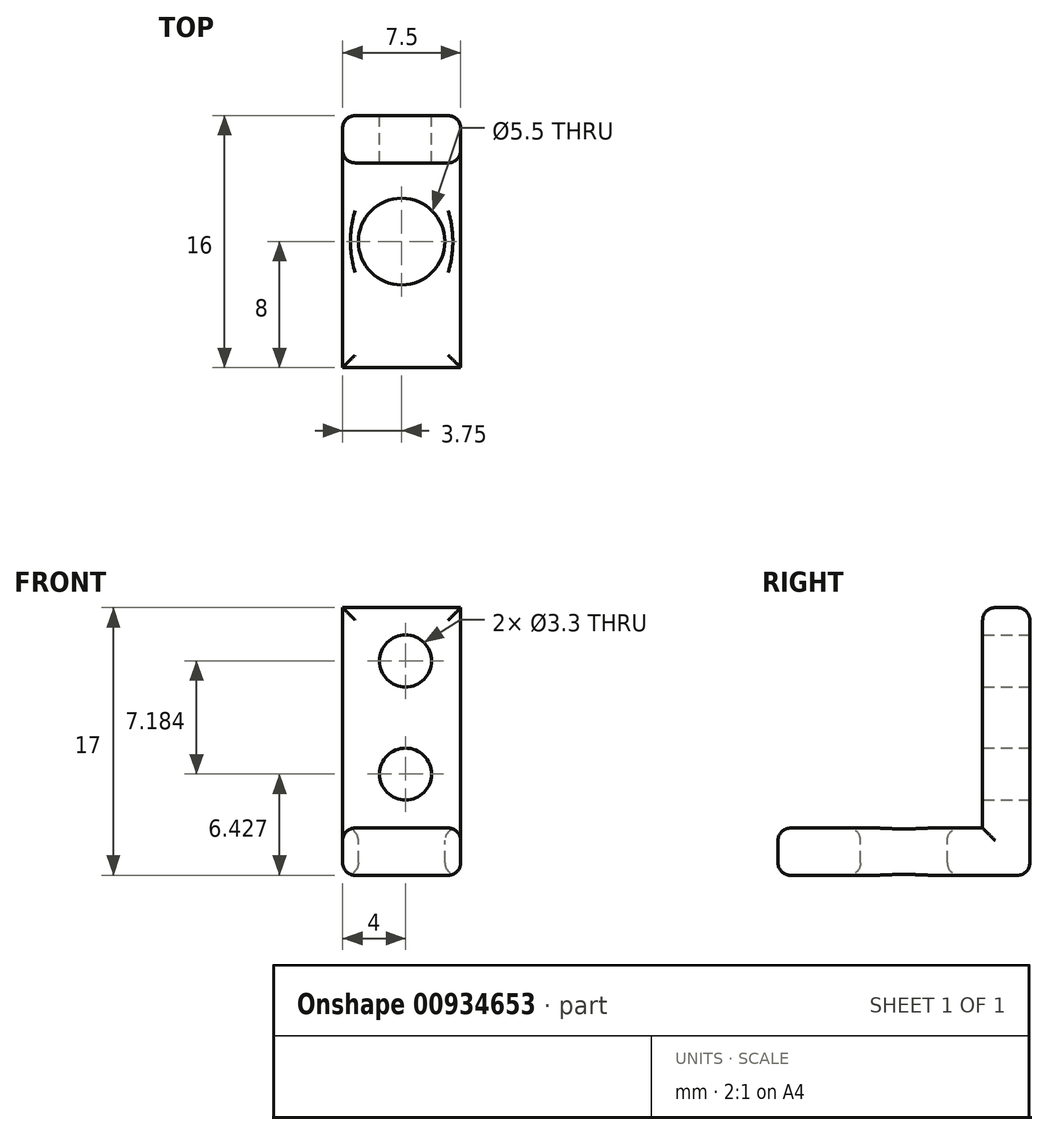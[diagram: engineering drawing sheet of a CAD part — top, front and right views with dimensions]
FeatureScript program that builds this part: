
annotation { "Feature Type Name" : "Feature", "Feature Type Description" : "" }
export const myFeature = defineFeature(function(context is Context, id is Id, definition is map)
    precondition{}
    {
        {
            var Q0;
            Q0=qCreatedBy(makeId("Top.planeOp"),FACE);
            var sketch = newSketch(context, id + "F0", { "sketchPlane" : qUnion([Q0])});
            skLineSegment(sketch, "E0.bottom", {"start": v(0, 0) * mm, "end": v(7.5, 0) * mm});
            skLineSegment(sketch, "E0.top", {"start": v(0, 16) * mm, "end": v(7.5, 16) * mm});
            skLineSegment(sketch, "E0.left", {"start": v(0, 0) * mm, "end": v(0, 16) * mm});
            skLineSegment(sketch, "E0.right", {"start": v(7.5, 0) * mm, "end": v(7.5, 16) * mm});
            skPoint(sketch, "E0.middle", {"position": v(3.75, 8) * mm});
            skCircle(sketch, "E1", {"center": v(3.75, 8) * mm, "radius": 2.75 * mm});
            skSolve(sketch);
        }
        {
            var Q0;
            Q0=makeQuery(id+"F0.imprint","IMPRINT",FACE,{"disambiguationData":[TD([[makeQuery(id+"F0.imprint","IMPRINT",EDGE,{"derivedFrom":sQuery(id+"F0.wireOp",EDGE,"E0.bottom")}),1.0]])]});
            var sketch = newSketch(context, id + "F1", { "sketchPlane" : qUnion([Q0])});
            skLineSegment(sketch, "E2.bottom", {"start": v(0, 13) * mm, "end": v(7.5, 13) * mm});
            skLineSegment(sketch, "E2.top", {"start": v(0, 16) * mm, "end": v(7.5, 16) * mm});
            skLineSegment(sketch, "E2.left", {"start": v(0, 13) * mm, "end": v(0, 16) * mm});
            skLineSegment(sketch, "E2.right", {"start": v(7.5, 13) * mm, "end": v(7.5, 16) * mm});
            skSolve(sketch);
        }
        {
            var Q0;
            Q0 = qSketchRegion(id + "F1", true);
            extrude(context, id + "F2", {"entities" : qUnion([Q0]), "depth" : 14 * mm, "offsetDistance" : 25 * mm});
        }
        {
            var Q0;
            Q0=makeQuery(id+"F0.imprint","IMPRINT",FACE,{"disambiguationData":[TD([[makeQuery(id+"F0.imprint","IMPRINT",EDGE,{"derivedFrom":sQuery(id+"F0.wireOp",EDGE,"E0.bottom")}),1.0]])]});
            extrude(context, id + "F3", {"entities" : qUnion([Q0]), "operationType" : NewBodyOperationType.ADD, "oppositeDirection" : true, "depth" : 3 * mm, "offsetDistance" : 25 * mm});
        }
        {
            var Q0;
            Q0=makeQuery(id+"F3.boolean.opBoolean","MERGE",FACE,{"derivedFrom":[makeQuery(id+"F2.opExtrude","SWEPT_FACE",FACE,{"disambiguationData":[OSD([sQuery(id+"F1.wireOp",EDGE,"E2.top")])]}),makeQuery(id+"F3.opExtrude","SWEPT_FACE",FACE,{"disambiguationData":[OSD([sQuery(id+"F0.wireOp",EDGE,"E0.top")])]})]});
            var sketch = newSketch(context, id + "F4", { "sketchPlane" : qUnion([Q0])});
            skCircle(sketch, "E3", {"center": v(-4, 3.43) * mm, "radius": 1.65 * mm});
            skCircle(sketch, "E4", {"center": v(-4, 10.61) * mm, "radius": 1.65 * mm});
            skSolve(sketch);
        }
        {
            var Q0;
            Q0 = qSketchRegion(id + "F4", true);
            extrude(context, id + "F5", {"entities" : qUnion([Q0]), "operationType" : NewBodyOperationType.REMOVE, "oppositeDirection" : true, "depth" : 25 * mm, "offsetDistance" : 25 * mm});
        }
        {
            var Q0;
            Q0=makeQuery(id+"F2.opExtrude","CAP_EDGE",EDGE,{"disambiguationData":[OSD([sQuery(id+"F1.wireOp",EDGE,"E2.top")])],"isStart":false});
            var Q1;
            Q1=makeQuery(id+"F2.opExtrude","CAP_EDGE",EDGE,{"disambiguationData":[OSD([sQuery(id+"F1.wireOp",EDGE,"E2.bottom")])],"isStart":false});
            var Q2;
            Q2=makeQuery(id+"F3.opExtrude","CAP_EDGE",EDGE,{"disambiguationData":[OSD([sQuery(id+"F0.wireOp",EDGE,"E0.bottom")])],"isStart":true});
            var Q3;
            Q3=makeQuery(id+"F3.opExtrude","CAP_EDGE",EDGE,{"disambiguationData":[OSD([sQuery(id+"F0.wireOp",EDGE,"E0.top")])],"isStart":false});
            var Q4;
            Q4=makeQuery(id+"F3.opExtrude","CAP_EDGE",EDGE,{"disambiguationData":[OSD([sQuery(id+"F0.wireOp",EDGE,"E0.bottom")])],"isStart":false});
            var Q5;
            Q5=makeQuery(id+"F5.boolean.opBoolean","COPY",EDGE,{"derivedFrom":makeQuery(id+"F5.opExtrude","CAP_EDGE",EDGE,{"disambiguationData":[OSD([sQuery(id+"F4.wireOp",EDGE,"E4")])],"isStart":true})});
            var Q6;
            Q6=makeQuery(id+"F5.boolean.opBoolean","COPY",EDGE,{"derivedFrom":makeQuery(id+"F5.opExtrude","CAP_EDGE",EDGE,{"disambiguationData":[OSD([sQuery(id+"F4.wireOp",EDGE,"E3")])],"isStart":true})});
            var Q7;
            Q7=makeQuery(id+"F3.opExtrude","CAP_EDGE",EDGE,{"disambiguationData":[OSD([sQuery(id+"F0.wireOp",EDGE,"E1")])],"isStart":false});
            var Q8;
            Q8=makeQuery(id+"F3.opExtrude","CAP_EDGE",EDGE,{"disambiguationData":[OSD([sQuery(id+"F0.wireOp",EDGE,"E1")])],"isStart":true});
            var Q9;
            Q9=makeQuery(id+"F3.boolean.opBoolean","MERGE",EDGE,{"derivedFrom":[makeQuery(id+"F2.opExtrude","SWEPT_EDGE",EDGE,{"disambiguationData":[OSD([sQuery(id+"F1.wireOp",EDGE,"E2.top"),sQuery(id+"F1.wireOp",EDGE,"E2.left")])]}),makeQuery(id+"F3.opExtrude","SWEPT_EDGE",EDGE,{"disambiguationData":[OSD([sQuery(id+"F0.wireOp",EDGE,"E0.top"),sQuery(id+"F0.wireOp",EDGE,"E0.left")])]})]});
            var Q10;
            Q10=makeQuery(id+"F3.boolean.opBoolean","MERGE",EDGE,{"derivedFrom":[makeQuery(id+"F2.opExtrude","SWEPT_EDGE",EDGE,{"disambiguationData":[OSD([sQuery(id+"F1.wireOp",EDGE,"E2.top"),sQuery(id+"F1.wireOp",EDGE,"E2.right")])]}),makeQuery(id+"F3.opExtrude","SWEPT_EDGE",EDGE,{"disambiguationData":[OSD([sQuery(id+"F0.wireOp",EDGE,"E0.top"),sQuery(id+"F0.wireOp",EDGE,"E0.right")])]})]});
            var Q11;
            Q11=makeQuery(id+"F3.opExtrude","CAP_EDGE",EDGE,{"disambiguationData":[OSD([sQuery(id+"F0.wireOp",EDGE,"E0.left")])],"isStart":false});
            var Q12;
            Q12=makeQuery(id+"F3.opExtrude","CAP_EDGE",EDGE,{"disambiguationData":[OSD([sQuery(id+"F0.wireOp",EDGE,"E0.right")])],"isStart":false});
            var Q13;
            Q13=makeQuery(id+"F3.opExtrude","CAP_EDGE",EDGE,{"disambiguationData":[OSD([sQuery(id+"F0.wireOp",EDGE,"E0.left")])],"isStart":true});
            var Q14;
            Q14=makeQuery(id+"F2.opExtrude","SWEPT_EDGE",EDGE,{"disambiguationData":[OSD([sQuery(id+"F0.wireOp",EDGE,"E0.left"),sQuery(id+"F1.wireOp",EDGE,"E2.bottom"),sQuery(id+"F1.wireOp",EDGE,"E2.left")])]});
            var Q15;
            Q15=makeQuery(id+"F3.opExtrude","CAP_EDGE",EDGE,{"disambiguationData":[OSD([sQuery(id+"F0.wireOp",EDGE,"E0.right")])],"isStart":true});
            var Q16;
            Q16=makeQuery(id+"F2.opExtrude","SWEPT_EDGE",EDGE,{"disambiguationData":[OSD([sQuery(id+"F0.wireOp",EDGE,"E0.right"),sQuery(id+"F1.wireOp",EDGE,"E2.bottom"),sQuery(id+"F1.wireOp",EDGE,"E2.right")])]});
            fillet(context, id + "F6", {"entities" : qUnion([Q0, Q1, Q2, Q3, Q4, Q5, Q6, Q7, Q8, Q9, Q10, Q11, Q12, Q13, Q14, Q15, Q16]), "radius" : 0.8 * mm, "tangentPropagation" : true, "allowEdgeOverflow" : false});
        }
    });
